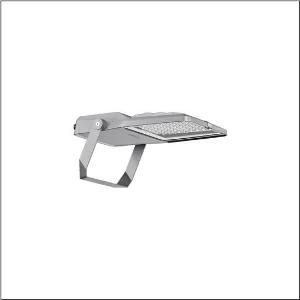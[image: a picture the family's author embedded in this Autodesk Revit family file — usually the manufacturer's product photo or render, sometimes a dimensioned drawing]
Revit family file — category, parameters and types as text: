
# Revit family: floodlight_fl_21_iq_mini___pl33t_5xa7772c3f1a_d349
name_source: partatom
category: Lighting Fixtures
units: mm (PartAtom-declared; Revit-internal decimal feet)

## family parameters
Cut with Voids When Loaded = No
Host = Face
Light Source = No
Part Type = Normal
Room Calculation Point = No
Round Connector Dimension = Use Diameter
Shared = No

## types (1)
- --- (1 x LED, 10390 lm, 87.2 W, 3000K)
    Apparent Load = 87 VA
    CIE Flux Codes = 26 75 99 100 100
    Color Rendering = 80
    Color Temperature = 3000K
    Default Elevation = 1800 mm
    Description = Floodlight FL 21 iQ mini, floodlight, primary light control with lens, of PMMA, primary optical cover: protective disc, of toughened safety glass, transparent, light distribution: PL33T, light emission: direct distribution, installation type: surface-mounted, lamps: LED, High Power LED, rated values: 10.390lm | 87,2W | 119,2lm/W (begin service life); end service life: 10.390lm | 92,1W; at 50% lumin. flux: 5.195lm | 40,1W | 129,6lm/W, colour temperature: 3000K, colour rendering: CRI > 80, light colour: 830, light setting 1 begin service life: 100% | 10.390lm | 87,2W | 119,2lm/W | 3.000K, light setting 1 end service life: 92,1W, further light settings possible, control: Street-Remote, Auto-Match, Temp-Guard, Night-Set, Smart-Wire, Desk-Remote (wireless, voltage-free reading and setting of iQ features in the workshop via application-optimized NFC function/RFID function), optimised constant luminous flux control (CLO 2.0), pre-setting: linear dimming characteristic, with terminal, 6-pole, mains connection: 220..240V, AC, 50/60Hz, luminaire housing, of diecast aluminium, powder-coated, SITECO metallic grey (DB 702S), corrosivity category C5 mid according to DIN EN ISO 12944suitable for swimming poolschlorine-resistant, sealing non-destructively replaceable, mounting bracket, of steel, galvanised, powder-coated, SITECO metallic grey (DB 702S), protection rating (complete): IP66, insulation class (complete): insulation class II (safety insulation), certification: CE, ENEC, VDE, protection symbol: D, impact resistance: IK08, permissible operating ambient temperature: -40..+40°C, permissible operating ambient temperature for outdoor applications: -40..+50°C, standard: DIN EN 12944, LABS conformity tested according to VDMA 24364:2018-05, packaging unit: 1 piece

Light Distribution: PL33T
    Height = 70 mm
    Lamp = 1 x LED
    Lamp Light Flux = 10390 lm
    Lamp Power = 87.2 W
    Lamp count = 1
    Length = 485 mm
    Luminous efficacy = 119 lm/W
    Manufacturer = Siteco
    ModVariant = No
    Model = 5XA7772C3F1A
    Mounting Place = Pole
    Mounting Type = Pole annexe
    Number of Poles = 1
    OnlyDefault = Yes
    Power Factor = 1
    Product Name = Floodlight FL 21 iQ mini | PL33T
    Product group = floodlight | pylon annexe
    ProductGroupID = 6201
    Protection Class = Protection class II
    Protection Degree = IP 66
    RLX_Detail_Level = 1
    RLX_Emergency_Light_Flux = 0 lm
    RLX_Emergency_Type = 0
    RLX_Emergency_Type_DB = No
    RlxData = <blob elided: 96409 chars, md5=1105f561>
    Socket = socket
    Standby Power = 0 W
    System Light Flux = 10390 lm
    System Power = 87 W
    Type Comments = factory setting: luminous flux: 100 % | dim-lin: 254 | 456 mA
    Type Image = l_1006845.jpg
    URL = http://relux.com
    VarID = @adj_150507
    Voltage = 0 V
    Weight = 0.00 kg
    Width = 337 mm

## geometry (parser evidence)
native form markers: Blend x4, Sweep x13
no freeform markers — native parametric forms only
